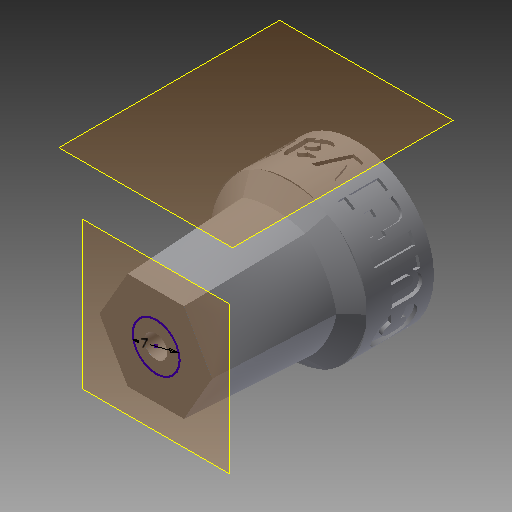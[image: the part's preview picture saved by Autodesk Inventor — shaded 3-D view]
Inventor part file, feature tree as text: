
AUTODESK INVENTOR PART (.ipt)
format: ipt  version: 2018 (Build 220112000, 112)  size: 697,856 bytes
history: native  units: mm
features: sketch x9, extrude x4, plane x2, projected_geometry x2, loft x1, chamfer x1, emboss x1
ambient origin geometry x8: Origin, YZ Plane, XZ Plane, XY Plane, X Axis, Y Axis, Z Axis, Center Point
bodies: Body1 (feature_tree)
feature tree (20):
  sketch  "Sketch3"  dims[d4=20.0mm d5=30.0mm]
  plane  "Work Plane1"
  loft  "Loft1"
  extrude  "Extrusion2"  TaperAngle=0.0deg  [1 undecoded]
  extrude  "Extrusion3"  Depth=20.0mm TaperAngle=0.0deg
  chamfer  "Chamfer1"  Distance=10.0mm
  sketch  "Sketch8"  dims[d23=0.5mm d24=0.0mm d25=10.0mm d26=0.0mm]
  plane  "Work Plane2"
  emboss  "Emboss1"
  extrude  "Extrusion4"  Depth=20.0mm
  sketch  "Sketch11"  dims[d29=20.0mm d30=0.0mm]
  extrude  "Extrusion5"  Depth=10.0mm TaperAngle=0.0deg
  sketch  "Sketch4"  dims[d6=0.0mm d7=90.0deg d8=0.0mm d9=90.0deg]
  sketch  "Sketch6"  dims[d13=3.4mm d14=20.0mm d15=0.0mm d16=10.0mm d17=0.0mm]
  sketch  "Sketch7"  dims[d19=2.3mm d20=2.0mm d21=45.0deg d22=20.0mm]
  projected_geometry  "Projected Loop1"
  sketch  "Sketch9"  dims[d27=7.0mm]
  sketch  "Sketch10"  dims[d28=7.0mm]
  projected_geometry  "Projected Loop2"
  sketch  "Sketch12"
note: 1 required parameter value undecoded (feature->parameter linkage not recoverable at this tier; creation-order binding heuristic only, values carry confidence <= 0.55)
